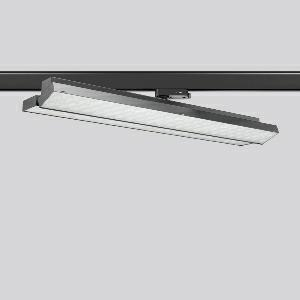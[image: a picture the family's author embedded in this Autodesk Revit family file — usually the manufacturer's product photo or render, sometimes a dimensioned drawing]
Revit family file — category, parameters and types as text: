
# Revit family: tx-move_742161_003_3_4fe5
name_source: partatom
category: Lighting Fixtures
units: mm (PartAtom-declared; Revit-internal decimal feet)

## family parameters
Cut with Voids When Loaded = No
Host = Face
Light Source = No
Part Type = Normal
Room Calculation Point = No
Round Connector Dimension = Use Diameter
Shared = No

## types (1)
- MultiLumen 1 (1 x LED Modul 835, 3025 lm, 3500)
    Apparent Load = 41 VA
    CIE Flux Codes = 88 96 99 100 100
    Color Rendering = 80
    Color Temperature = 3500
    Default Elevation = 1800 mm
    Description = Series: TX-MOVE
Multifunctional surface-mounted spotlight for area lighting. Very flat design. Housing: sheet steel, powder-coated. Rotation range: 356°. Swivel range: 90°. Consistent alignment possible with visible tilt scale. High-efficiency LED units with optimum light control thanks to clear plastic (PC) lens optics. Spezielle Mikrostrukturen reduzieren Gelbsaum. Symmetrical light distribution. With multi adaptor for 3-circuit tracks 230 V. Suitable for Track on ceiling. MultiLumen: Luminous flux adjustable in 3 steps. Factory setting is the highest luminous flux. Environmentally friendly and resource-saving due to replaceable and recyclable components. 
Colour: deep black, matt (RAL 9005)
Length: 570 mm
Width: 119 mm
Height: 92 mm
Lamp: LED
Socket: without socket
Colour temperature: 3500K
Colour rendering index (CRI): 80
System power: 41 W
Rated luminous flux: 6050 lm
Luminous efficiency: 148 lm/W
System power 2: 57 W
Rated luminous flux 2: 8200 lm
Luminous efficiency 2: 144 lm/W
System power 3: 73 W
Rated luminous flux 3: 10000 lm
Luminous efficiency 3: 137 lm/W
Control gear: Regulated power supply
Protection class: I
Type of protection: IP 20
    Height = 75 mm
    Lamp = 1 x LED Modul 835
    Lamp Light Flux = 3025 lm
    Lamp count = 1
    Length = 569 mm
    Lifetime = 50000 h
    Luminous efficacy = 148 lm/W
    Manufacturer = RZB
    ModVariant = No
    Model = 742161.003.3
    Mounting Place = Ceiling
    Mounting Type = Rail mounted
    Number of Poles = 1
    OnlyDefault = Yes
    Power Factor = 1
    Product Name = TX-MOVE
    Product group = Track mounted projectors
    ProductGroupID = 301
    Protection Class = Protection class I
    Protection Degree = IP 20
    RLX_Detail_Level = 1
    RLX_Emergency_Light_Flux = 0 lm
    RLX_Emergency_Type = 0
    RLX_Emergency_Type_DB = No
    RlxData = <blob elided: 36813 chars, md5=1c0599d3>
    Socket = socket
    Standby Power = 0 W
    System Light Flux = 6050 lm
    System Power = 41 W
    Type Comments = MultiLumen 1
    Type Image = 742162.003.jpg
    URL = http://relux.com
    VarID = multilumen_1
    Voltage = 230 V
    Voltage Range = 220-240 V
    Weight = 0.00 kg
    Width = 119 mm

## geometry (parser evidence)
native form markers: Blend x4, Sweep x14
no freeform markers — native parametric forms only
